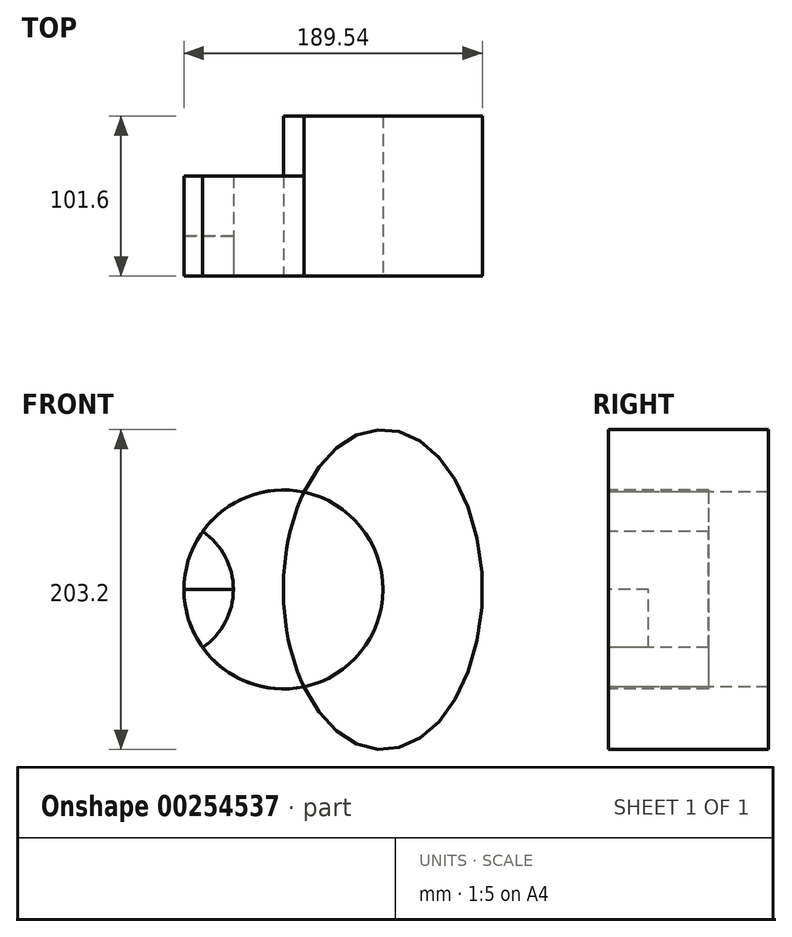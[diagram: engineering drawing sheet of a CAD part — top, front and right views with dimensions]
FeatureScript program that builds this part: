
annotation { "Feature Type Name" : "Feature", "Feature Type Description" : "" }
export const myFeature = defineFeature(function(context is Context, id is Id, definition is map)
    precondition{}
    {
        {
            var Q0;
            Q0=qCreatedBy(makeId("Front.planeOp"),FACE);
            var sketch = newSketch(context, id + "F0", { "sketchPlane" : qUnion([Q0])});
            skLineSegment(sketch, "E0", {"start": v(0, 0) * mm, "end": v(-76.2, 0) * mm});
            skCircle(sketch, "E1", {"center": v(-76.2, 0) * mm, "radius": 44.45 * mm});
            skLineSegment(sketch, "E2", {"start": v(63.18, 0) * mm, "end": v(63.18, 101.6) * mm});
            skEllipse(sketch, "E3", {"center": v(63.18, 0) * mm, "majorRadius": 63.18 * mm, "minorRadius": 101.6 * mm, "majorAxis": v(-1, 0)});
            skLineSegment(sketch, "E4", {"start": v(-31.75, 0) * mm, "end": v(-63.5, 0) * mm});
            skLineSegment(sketch, "E5", {"start": v(0, 0) * mm, "end": v(31.75, 0) * mm});
            skCircle(sketch, "E6", {"center": v(0, 0) * mm, "radius": 63.18 * mm});
            skSolve(sketch);
        }
        {
            var Q0;
            {var subQ0=sQuery(id+"F0.wireOp",EDGE,"riXvawn5-wCje-mGZ3-hzxN-7X7dYMWwSy2O");var subQ1=sQuery(id+"F0.wireOp",EDGE,"E0");var subQ2=makeQuery(id+"F0.imprint","INTERSECT",VERTEX,{"derivedFrom":[subQ1,subQ0]});Q0=makeQuery(id+"F0.imprint","IMPRINT",FACE,{"disambiguationData":[TD([[makeQuery(id+"F0.imprint","IMPRINT",EDGE,{"disambiguationData":[TD([[subQ2,1.0]])],"derivedFrom":subQ1}),-1.0]])]});}
            var Q1;
            {var subQ0=sQuery(id+"F0.wireOp",EDGE,"riXvawn5-wCje-mGZ3-hzxN-7X7dYMWwSy2O");var subQ1=sQuery(id+"F0.wireOp",EDGE,"E0");var subQ2=makeQuery(id+"F0.imprint","INTERSECT",VERTEX,{"derivedFrom":[subQ1,subQ0]});Q1=makeQuery(id+"F0.imprint","IMPRINT",FACE,{"disambiguationData":[TD([[makeQuery(id+"F0.imprint","IMPRINT",EDGE,{"disambiguationData":[TD([[subQ2,1.0]])],"derivedFrom":subQ1}),1.0]])]});}
            var Q2;
            {var subQ0=sQuery(id+"F0.wireOp",EDGE,"E3");var subQ1=sQuery(id+"F0.wireOp",EDGE,"E0");var subQ2=makeQuery(id+"F0.imprint","INTERSECT",VERTEX,{"derivedFrom":[subQ1,subQ0]});Q2=makeQuery(id+"F0.imprint","IMPRINT",FACE,{"disambiguationData":[TD([[makeQuery(id+"F0.imprint","IMPRINT",EDGE,{"disambiguationData":[TD([[subQ2,-1.0]])],"derivedFrom":subQ1}),1.0]])]});}
            var Q3;
            {var subQ0=sQuery(id+"F0.wireOp",EDGE,"E3");var subQ1=sQuery(id+"F0.wireOp",EDGE,"E0");var subQ2=makeQuery(id+"F0.imprint","INTERSECT",VERTEX,{"derivedFrom":[subQ1,subQ0]});Q3=makeQuery(id+"F0.imprint","IMPRINT",FACE,{"disambiguationData":[TD([[makeQuery(id+"F0.imprint","IMPRINT",EDGE,{"disambiguationData":[TD([[subQ2,-1.0]])],"derivedFrom":subQ1}),-1.0]])]});}
            extrude(context, id + "F1", {"entities" : qUnion([Q0, Q1, Q2, Q3]), "oppositeDirection" : true, "depth" : 63.5 * mm});
        }
        {
            var Q0;
            {var subQ0=sQuery(id+"F0.wireOp",EDGE,"E2");Q0=makeQuery(id+"F0.imprint","IMPRINT",FACE,{"disambiguationData":[TD([[makeQuery(id+"F0.imprint","IMPRINT",EDGE,{"derivedFrom":subQ0}),-1.0]])]});}
            var Q1;
            {var subQ0=sQuery(id+"F0.wireOp",EDGE,"E2");Q1=makeQuery(id+"F0.imprint","IMPRINT",FACE,{"disambiguationData":[TD([[makeQuery(id+"F0.imprint","IMPRINT",EDGE,{"derivedFrom":subQ0}),1.0]])]});}
            extrude(context, id + "F2", {"entities" : qUnion([Q0, Q1]), "oppositeDirection" : true, "depth" : 101.6 * mm});
        }
        {
            var Q0;
            {var subQ0=sQuery(id+"F0.wireOp",EDGE,"riXvawn5-wCje-mGZ3-hzxN-7X7dYMWwSy2O");var subQ1=sQuery(id+"F0.wireOp",EDGE,"E1");var subQ2=makeQuery(id+"F0.imprint","INTERSECT",VERTEX,{"disambiguationData":[OD(0.0)],"derivedFrom":[subQ1,subQ0]});Q0=makeQuery(id+"F0.imprint","IMPRINT",FACE,{"disambiguationData":[TD([[makeQuery(id+"F0.imprint","IMPRINT",EDGE,{"disambiguationData":[TD([[subQ2,-1.0]])],"derivedFrom":subQ1}),1.0]])]});}
            extrude(context, id + "F3", {"entities" : qUnion([Q0]), "oppositeDirection" : true, "depth" : 25.4 * mm});
        }
        {
            var Q0;
            {var subQ1=sQuery(id+"F0.wireOp",EDGE,"E1");var subQ3=sQuery(id+"F0.wireOp",EDGE,"E6");var subQ4=makeQuery(id+"F0.imprint","INTERSECT",VERTEX,{"disambiguationData":[OD(1.0)],"derivedFrom":[subQ1,subQ3]});Q0=makeQuery(id+"F0.imprint","IMPRINT",FACE,{"disambiguationData":[TD([[makeQuery(id+"F0.imprint","IMPRINT",EDGE,{"disambiguationData":[TD([[subQ4,1.0]])],"derivedFrom":subQ3}),1.0]])]});}
            var Q1;
            {var subQ1=sQuery(id+"F0.wireOp",EDGE,"E1");var subQ3=sQuery(id+"F0.wireOp",EDGE,"E6");var subQ4=makeQuery(id+"F0.imprint","INTERSECT",VERTEX,{"disambiguationData":[OD(0.0)],"derivedFrom":[subQ1,subQ3]});Q1=makeQuery(id+"F0.imprint","IMPRINT",FACE,{"disambiguationData":[TD([[makeQuery(id+"F0.imprint","IMPRINT",EDGE,{"disambiguationData":[TD([[subQ4,-1.0]])],"derivedFrom":subQ3}),1.0]])]});}
            extrude(context, id + "F4", {"entities" : qUnion([Q0, Q1]), "oppositeDirection" : true, "depth" : 63.5 * mm});
        }
        {
            var Q0;
            {var subQ0=sQuery(id+"F0.wireOp",EDGE,"E3");var subQ1=makeQuery(id+"F0.imprint","INTERSECT",VERTEX,{"derivedFrom":[sQuery(id+"F0.wireOp",EDGE,"E0"),subQ0]});Q0=makeQuery(id+"F0.imprint","IMPRINT",FACE,{"disambiguationData":[TD([[makeQuery(id+"F0.imprint","IMPRINT",EDGE,{"disambiguationData":[TD([[subQ1,1.0]])],"derivedFrom":subQ0}),1.0]])]});}
            extrude(context, id + "F5", {"entities" : qUnion([Q0]), "oppositeDirection" : true, "depth" : 101.6 * mm});
        }
    });
